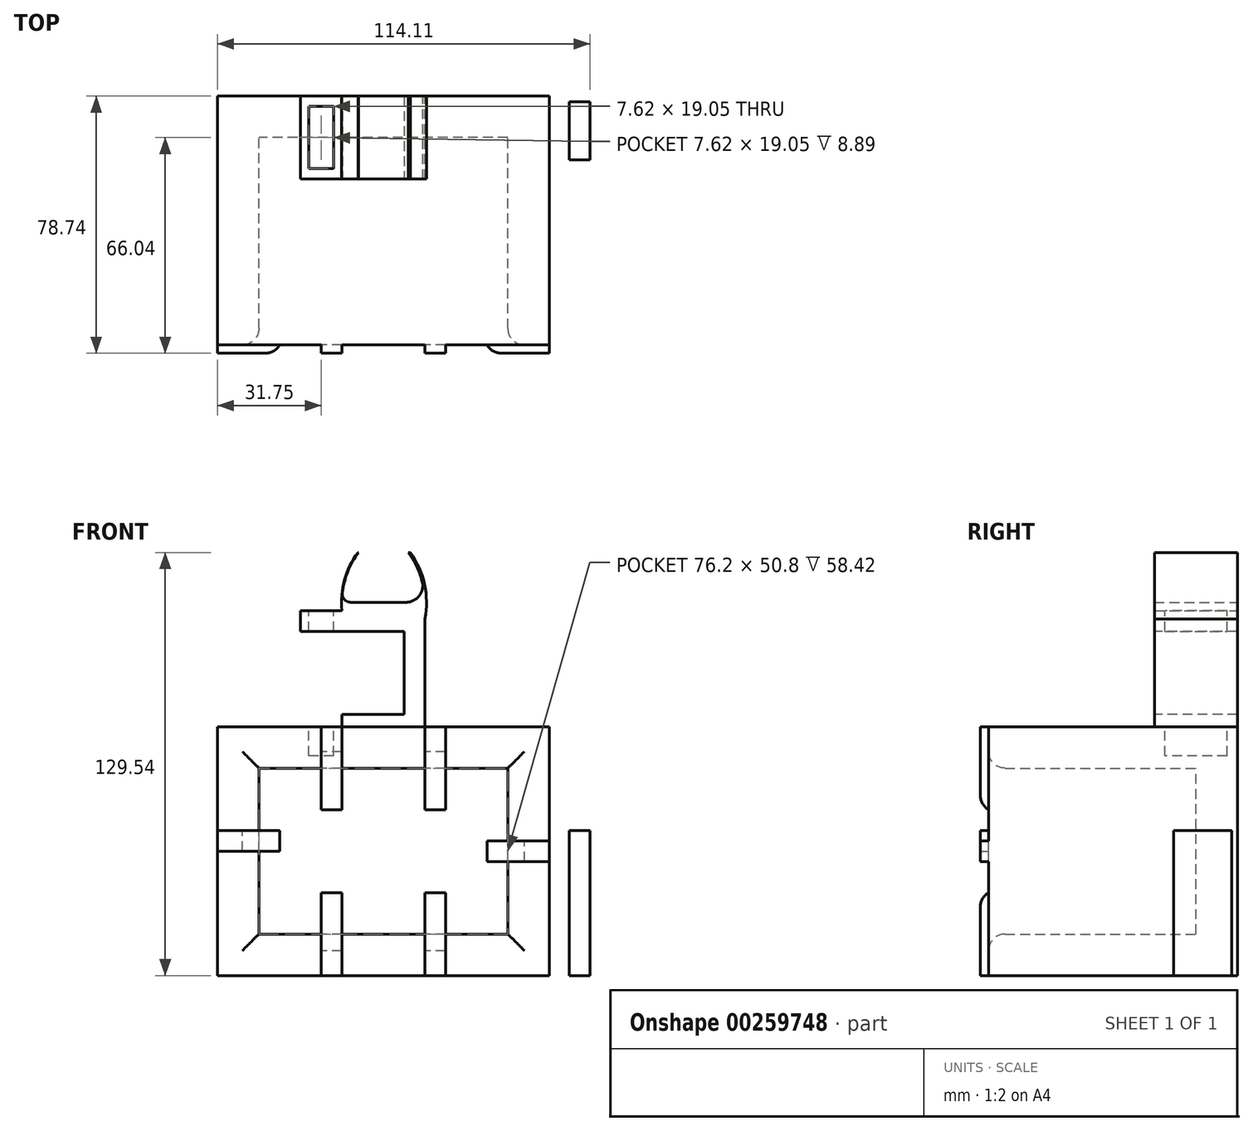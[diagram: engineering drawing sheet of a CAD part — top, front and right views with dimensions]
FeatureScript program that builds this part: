
annotation { "Feature Type Name" : "Feature", "Feature Type Description" : "" }
export const myFeature = defineFeature(function(context is Context, id is Id, definition is map)
    precondition{}
    {
        {
            var Q0;
            Q0=qCreatedBy(makeId("Front.planeOp"),FACE);
            var sketch = newSketch(context, id + "F0", { "sketchPlane" : qUnion([Q0])});
            skLineSegment(sketch, "E0.bottom", {"start": v(0, 0) * mm, "end": v(-101.6, 0) * mm});
            skLineSegment(sketch, "E0.top", {"start": v(0, 76.2) * mm, "end": v(-101.6, 76.2) * mm});
            skLineSegment(sketch, "E0.left", {"start": v(0, 0) * mm, "end": v(0, 76.2) * mm});
            skLineSegment(sketch, "E0.right", {"start": v(-101.6, 0) * mm, "end": v(-101.6, 76.2) * mm});
            skSolve(sketch);
        }
        {
            var Q0;
            Q0=makeQuery(id+"F0.imprint","IMPRINT",FACE,{"disambiguationData":[TD([[makeQuery(id+"F0.imprint","IMPRINT",EDGE,{"derivedFrom":sQuery(id+"F0.wireOp",EDGE,"E0.bottom")}),-1.0]])]});
            extrude(context, id + "F1", {"entities" : qUnion([Q0]), "depth" : 76.2 * mm});
        }
        {
            var Q0;
            Q0=makeQuery(id+"F1.opExtrude","CAP_FACE",FACE,{"disambiguationData":[OSD([sQuery(id+"F0.wireOp",EDGE,"E0.bottom"),sQuery(id+"F0.wireOp",EDGE,"E0.top"),sQuery(id+"F0.wireOp",EDGE,"E0.left"),sQuery(id+"F0.wireOp",EDGE,"E0.right")])],"isStart":false});
            shell(context, id + "F2", {"entities" : qUnion([Q0]), "thickness" : 12.7 * mm});
        }
        {
            var Q0;
            {var subQ0=sQuery(id+"F0.wireOp",EDGE,"E0.right");Q0=makeQuery(id+"F2.opShell","OFFSET_EDGE",EDGE,{"disambiguationData":[OSD([subQ0]),TDD([makeQuery(id+"F1.opExtrude","CAP_EDGE",EDGE,{"disambiguationData":[OSD([subQ0])],"isStart":false})])]});}
            var Q1;
            {var subQ0=sQuery(id+"F0.wireOp",EDGE,"E0.top");Q1=makeQuery(id+"F2.opShell","OFFSET_EDGE",EDGE,{"disambiguationData":[OSD([subQ0]),TDD([makeQuery(id+"F1.opExtrude","CAP_EDGE",EDGE,{"disambiguationData":[OSD([subQ0])],"isStart":false})])]});}
            var Q2;
            {var subQ0=sQuery(id+"F0.wireOp",EDGE,"E0.left");Q2=makeQuery(id+"F2.opShell","OFFSET_EDGE",EDGE,{"disambiguationData":[OSD([subQ0]),TDD([makeQuery(id+"F1.opExtrude","CAP_EDGE",EDGE,{"disambiguationData":[OSD([subQ0])],"isStart":false})])]});}
            var Q3;
            {var subQ0=sQuery(id+"F0.wireOp",EDGE,"E0.bottom");Q3=makeQuery(id+"F2.opShell","OFFSET_EDGE",EDGE,{"disambiguationData":[OSD([subQ0]),TDD([makeQuery(id+"F1.opExtrude","CAP_EDGE",EDGE,{"disambiguationData":[OSD([subQ0])],"isStart":false})])]});}
            fillet(context, id + "F3", {"entities" : qUnion([Q0, Q1, Q2, Q3]), "radius" : 5.08 * mm, "tangentPropagation" : true, "allowEdgeOverflow" : false});
        }
        {
            var Q0;
            Q0=makeQuery(id+"F1.opExtrude","CAP_FACE",FACE,{"disambiguationData":[OSD([sQuery(id+"F0.wireOp",EDGE,"E0.bottom"),sQuery(id+"F0.wireOp",EDGE,"E0.top"),sQuery(id+"F0.wireOp",EDGE,"E0.left"),sQuery(id+"F0.wireOp",EDGE,"E0.right")])],"isStart":false});
            var sketch = newSketch(context, id + "F4", { "sketchPlane" : qUnion([Q0])});
            skLineSegment(sketch, "E1.bottom", {"start": v(-69.85, 76.2) * mm, "end": v(-63.5, 76.2) * mm});
            skLineSegment(sketch, "E1.top", {"start": v(-69.85, 50.8) * mm, "end": v(-63.5, 50.8) * mm});
            skLineSegment(sketch, "E1.left", {"start": v(-69.85, 76.2) * mm, "end": v(-69.85, 50.8) * mm});
            skLineSegment(sketch, "E1.right", {"start": v(-63.5, 76.2) * mm, "end": v(-63.5, 50.8) * mm});
            skLineSegment(sketch, "E2.bottom", {"start": v(-38.1, 76.2) * mm, "end": v(-31.75, 76.2) * mm});
            skLineSegment(sketch, "E2.top", {"start": v(-38.1, 50.8) * mm, "end": v(-31.75, 50.8) * mm});
            skLineSegment(sketch, "E2.left", {"start": v(-38.1, 76.2) * mm, "end": v(-38.1, 50.8) * mm});
            skLineSegment(sketch, "E2.right", {"start": v(-31.75, 76.2) * mm, "end": v(-31.75, 50.8) * mm});
            skLineSegment(sketch, "E3.bottom", {"start": v(-101.6, 38.1) * mm, "end": v(-82.55, 38.1) * mm});
            skLineSegment(sketch, "E3.top", {"start": v(-101.6, 44.45) * mm, "end": v(-82.55, 44.45) * mm});
            skLineSegment(sketch, "E3.left", {"start": v(-101.6, 38.1) * mm, "end": v(-101.6, 44.45) * mm});
            skLineSegment(sketch, "E3.right", {"start": v(-82.55, 38.1) * mm, "end": v(-82.55, 44.45) * mm});
            skLineSegment(sketch, "E4.bottom", {"start": v(-12.7, 41.27) * mm, "end": v(0, 41.27) * mm});
            skLineSegment(sketch, "E4.top", {"start": v(-19.05, 34.92) * mm, "end": v(0, 34.92) * mm});
            skLineSegment(sketch, "E4.right", {"start": v(0, 41.27) * mm, "end": v(0, 34.92) * mm});
            skLineSegment(sketch, "E5.bottom", {"start": v(-69.85, 0) * mm, "end": v(-63.5, 0) * mm});
            skLineSegment(sketch, "E5.top", {"start": v(-69.85, 25.4) * mm, "end": v(-63.5, 25.4) * mm});
            skLineSegment(sketch, "E5.left", {"start": v(-69.85, 0) * mm, "end": v(-69.85, 25.4) * mm});
            skLineSegment(sketch, "E5.right", {"start": v(-63.5, 0) * mm, "end": v(-63.5, 25.4) * mm});
            skLineSegment(sketch, "E6.bottom", {"start": v(-38.1, 25.4) * mm, "end": v(-31.75, 25.4) * mm});
            skLineSegment(sketch, "E6.top", {"start": v(-38.1, 0) * mm, "end": v(-31.75, 0) * mm});
            skLineSegment(sketch, "E6.left", {"start": v(-38.1, 25.4) * mm, "end": v(-38.1, 0) * mm});
            skLineSegment(sketch, "E6.right", {"start": v(-31.75, 25.4) * mm, "end": v(-31.75, 0) * mm});
            skLineSegment(sketch, "E7", {"start": v(-12.7, 41.27) * mm, "end": v(-19.05, 41.27) * mm});
            skLineSegment(sketch, "E8", {"start": v(-19.05, 41.27) * mm, "end": v(-19.05, 34.92) * mm});
            skSolve(sketch);
        }
        {
            var Q0;
            Q0 = qSketchRegion(id + "F4", true);
            extrude(context, id + "F5", {"entities" : qUnion([Q0]), "operationType" : NewBodyOperationType.ADD, "depth" : 2.54 * mm});
        }
        {
            var Q0;
            Q0=makeQuery(id+"F5.opExtrude","CAP_EDGE",EDGE,{"disambiguationData":[OSD([sQuery(id+"F4.wireOp",EDGE,"E3.right")])],"isStart":false});
            var Q1;
            Q1=makeQuery(id+"F5.opExtrude","CAP_EDGE",EDGE,{"disambiguationData":[OSD([sQuery(id+"F4.wireOp",EDGE,"E1.top")])],"isStart":false});
            var Q2;
            Q2=makeQuery(id+"F5.opExtrude","CAP_EDGE",EDGE,{"disambiguationData":[OSD([sQuery(id+"F4.wireOp",EDGE,"E2.top")])],"isStart":false});
            var Q3;
            Q3=makeQuery(id+"F5.opExtrude","CAP_EDGE",EDGE,{"disambiguationData":[OSD([sQuery(id+"F4.wireOp",EDGE,"E8")])],"isStart":false});
            var Q4;
            Q4=makeQuery(id+"F5.opExtrude","CAP_EDGE",EDGE,{"disambiguationData":[OSD([sQuery(id+"F4.wireOp",EDGE,"E6.bottom")])],"isStart":false});
            var Q5;
            Q5=makeQuery(id+"F5.opExtrude","CAP_EDGE",EDGE,{"disambiguationData":[OSD([sQuery(id+"F4.wireOp",EDGE,"E5.top")])],"isStart":false});
            fillet(context, id + "F6", {"entities" : qUnion([Q0, Q1, Q2, Q3, Q4, Q5]), "radius" : 5.08 * mm, "tangentPropagation" : true, "allowEdgeOverflow" : false});
        }
        {
            var Q0;
            Q0=makeQuery(id+"F1.opExtrude","CAP_FACE",FACE,{"disambiguationData":[OSD([sQuery(id+"F0.wireOp",EDGE,"E0.bottom"),sQuery(id+"F0.wireOp",EDGE,"E0.top"),sQuery(id+"F0.wireOp",EDGE,"E0.left"),sQuery(id+"F0.wireOp",EDGE,"E0.right")])],"isStart":true});
            var sketch = newSketch(context, id + "F7", { "sketchPlane" : qUnion([Q0])});
            skLineSegment(sketch, "E9.bottom", {"start": v(38.1, 76.2) * mm, "end": v(63.5, 76.2) * mm});
            skLineSegment(sketch, "E9.top", {"start": v(38.1, 114.3) * mm, "end": v(63.5, 114.3) * mm});
            skLineSegment(sketch, "E9.left", {"start": v(38.1, 76.2) * mm, "end": v(38.1, 114.3) * mm});
            skLineSegment(sketch, "E9.right", {"start": v(63.5, 76.2) * mm, "end": v(63.5, 114.3) * mm});
            skSolve(sketch);
        }
        {
            var Q0;
            Q0 = qSketchRegion(id + "F7", true);
            extrude(context, id + "F8", {"entities" : qUnion([Q0]), "operationType" : NewBodyOperationType.ADD, "oppositeDirection" : true, "depth" : 25.4 * mm});
        }
        {
            var Q0;
            Q0=makeQuery(id+"F8.opExtrude","SWEPT_FACE",FACE,{"disambiguationData":[OSD([sQuery(id+"F7.wireOp",EDGE,"E9.right")])]});
            var sketch = newSketch(context, id + "F9", { "sketchPlane" : qUnion([Q0])});
            skLineSegment(sketch, "E10.bottom", {"start": v(25.4, 114.3) * mm, "end": v(0, 114.3) * mm});
            skLineSegment(sketch, "E10.top", {"start": v(25.4, 111.76) * mm, "end": v(0, 111.76) * mm});
            skLineSegment(sketch, "E10.left", {"start": v(25.4, 114.3) * mm, "end": v(25.4, 111.76) * mm});
            skLineSegment(sketch, "E10.right", {"start": v(0, 114.3) * mm, "end": v(0, 111.76) * mm});
            skSolve(sketch);
        }
        {
            var Q0;
            Q0 = qSketchRegion(id + "F9", true);
            var Q1;
            Q1=makeQuery(id+"F8.opExtrude","SWEPT_EDGE",EDGE,{"disambiguationData":[OSD([sQuery(id+"F7.wireOp",EDGE,"E9.top"),sQuery(id+"F7.wireOp",EDGE,"E9.left")])]});
            revolve(context, id + "F10", {"operationType" : NewBodyOperationType.ADD, "entities" : qUnion([Q0]), "axis" : qUnion([Q1]), "revolveType" : RevolveType.ONE_DIRECTION, "angle" : 45 * degree});
        }
        {
            var Q0;
            Q0=makeQuery(id+"F8.opExtrude","SWEPT_FACE",FACE,{"disambiguationData":[OSD([sQuery(id+"F7.wireOp",EDGE,"E9.left")])]});
            var sketch = newSketch(context, id + "F11", { "sketchPlane" : qUnion([Q0])});
            skLineSegment(sketch, "E11.bottom", {"start": v(-25.4, 114.3) * mm, "end": v(0, 114.3) * mm});
            skLineSegment(sketch, "E11.top", {"start": v(-25.4, 109.22) * mm, "end": v(0, 109.22) * mm});
            skLineSegment(sketch, "E11.left", {"start": v(-25.4, 114.3) * mm, "end": v(-25.4, 109.22) * mm});
            skLineSegment(sketch, "E11.right", {"start": v(0, 114.3) * mm, "end": v(0, 109.22) * mm});
            skSolve(sketch);
        }
        {
            var Q0;
            Q0 = qSketchRegion(id + "F11", true);
            var Q1;
            Q1=makeQuery(id+"F8.opExtrude","SWEPT_EDGE",EDGE,{"disambiguationData":[OSD([sQuery(id+"F7.wireOp",EDGE,"E9.top"),sQuery(id+"F7.wireOp",EDGE,"E9.right")])]});
            revolve(context, id + "F12", {"operationType" : NewBodyOperationType.ADD, "entities" : qUnion([Q0]), "axis" : qUnion([Q1]), "revolveType" : RevolveType.ONE_DIRECTION, "oppositeDirection" : true, "angle" : 60 * degree});
        }
        {
            var Q0;
            Q0=makeQuery(id+"F8.opExtrude","SWEPT_FACE",FACE,{"disambiguationData":[OSD([sQuery(id+"F7.wireOp",EDGE,"E9.top")])]});
            extrude(context, id + "F13", {"entities" : qUnion([Q0]), "operationType" : NewBodyOperationType.REMOVE, "depth" : 25.4 * mm, "hasSecondDirection" : true, "secondDirectionOppositeDirection" : false, "secondDirectionDepth" : 15.24 * mm});
        }
        {
            var Q0;
            Q0=makeQuery(id+"F10.boolean.opBoolean","MERGE",EDGE,{"derivedFrom":[makeQuery(id+"F8.opExtrude","SWEPT_EDGE",EDGE,{"disambiguationData":[OSD([sQuery(id+"F7.wireOp",EDGE,"E9.top"),sQuery(id+"F7.wireOp",EDGE,"E9.right")])]}),makeQuery(id+"F10.opRevolve","CAP_EDGE",EDGE,{"disambiguationData":[OSD([sQuery(id+"F9.wireOp",EDGE,"E10.bottom")]),OD(0.0)],"isStart":false})]});
            fillet(context, id + "F14", {"entities" : qUnion([Q0]), "radius" : 2.54 * mm, "tangentPropagation" : true, "allowEdgeOverflow" : false});
        }
        {
            var Q0;
            Q0=makeQuery(id+"F12.boolean.opBoolean","MERGE",EDGE,{"derivedFrom":[makeQuery(id+"F8.opExtrude","SWEPT_EDGE",EDGE,{"disambiguationData":[OSD([sQuery(id+"F7.wireOp",EDGE,"E9.top"),sQuery(id+"F7.wireOp",EDGE,"E9.left")])]}),makeQuery(id+"F12.opRevolve","CAP_EDGE",EDGE,{"disambiguationData":[OSD([sQuery(id+"F11.wireOp",EDGE,"E11.bottom")]),OD(0.0)],"isStart":false})]});
            fillet(context, id + "F15", {"entities" : qUnion([Q0]), "radius" : 5.08 * mm, "tangentPropagation" : true, "allowEdgeOverflow" : false});
        }
        {
            var Q0;
            Q0=makeQuery(id+"F8.opExtrude","SWEPT_FACE",FACE,{"disambiguationData":[OSD([sQuery(id+"F7.wireOp",EDGE,"E9.right")])]});
            var sketch = newSketch(context, id + "F16", { "sketchPlane" : qUnion([Q0])});
            skLineSegment(sketch, "E12.bottom", {"start": v(0, 80) * mm, "end": v(25.4, 80) * mm});
            skLineSegment(sketch, "E12.top", {"start": v(0, 105.4) * mm, "end": v(25.4, 105.4) * mm});
            skLineSegment(sketch, "E12.left", {"start": v(0, 80) * mm, "end": v(0, 105.4) * mm});
            skLineSegment(sketch, "E12.right", {"start": v(25.4, 80) * mm, "end": v(25.4, 105.4) * mm});
            skSolve(sketch);
        }
        {
            var Q0;
            Q0 = qSketchRegion(id + "F16", true);
            extrude(context, id + "F17", {"entities" : qUnion([Q0]), "operationType" : NewBodyOperationType.REMOVE, "oppositeDirection" : true, "depth" : 19.05 * mm});
        }
        {
            var Q0;
            {var subQ0=sQuery(id+"F7.wireOp",EDGE,"E9.right");Q0=makeQuery(id+"F17.boolean.opBoolean","SPLIT",FACE,{"disambiguationData":[TD([makeQuery(id+"F10.opRevolve","SWEPT_FACE",FACE,{"disambiguationData":[OSD([sQuery(id+"F9.wireOp",EDGE,"E10.top")])]})])],"derivedFrom":makeQuery(id+"F8.opExtrude","SWEPT_FACE",FACE,{"disambiguationData":[OSD([subQ0])]})});}
            extrude(context, id + "F18", {"entities" : qUnion([Q0]), "operationType" : NewBodyOperationType.ADD, "depth" : 12.7 * mm});
        }
        {
            var Q0;
            Q0=makeQuery(id+"F18.opExtrude","SWEPT_FACE",FACE,{"disambiguationData":[OSD([sQuery(id+"F9.wireOp",EDGE,"E10.top")])]});
            var sketch = newSketch(context, id + "F19", { "sketchPlane" : qUnion([Q0])});
            skCircle(sketch, "E13", {"center": v(-69.85, -12.7) * mm, "radius": 3.81 * mm});
            skLineSegment(sketch, "E14.bottom", {"start": v(-66.04, -3.18) * mm, "end": v(-73.66, -3.18) * mm});
            skLineSegment(sketch, "E14.top", {"start": v(-66.04, -22.23) * mm, "end": v(-73.66, -22.23) * mm});
            skLineSegment(sketch, "E14.left", {"start": v(-66.04, -3.18) * mm, "end": v(-66.04, -22.23) * mm});
            skLineSegment(sketch, "E14.right", {"start": v(-73.66, -3.18) * mm, "end": v(-73.66, -22.23) * mm});
            skSolve(sketch);
        }
        {
            var Q0;
            Q0 = qSketchRegion(id + "F19", true);
            extrude(context, id + "F20", {"entities" : qUnion([Q0]), "operationType" : NewBodyOperationType.REMOVE, "oppositeDirection" : true, "depth" : 44.45 * mm});
        }
        {
            var Q0;
            Q0=qCreatedBy(makeId("Top.planeOp"),FACE);
            var sketch = newSketch(context, id + "F21", { "sketchPlane" : qUnion([Q0])});
            skLineSegment(sketch, "E15.bottom", {"start": v(12.5, -19.56) * mm, "end": v(6.16, -19.56) * mm});
            skLineSegment(sketch, "E15.top", {"start": v(12.5, -1.78) * mm, "end": v(6.16, -1.78) * mm});
            skLineSegment(sketch, "E15.left", {"start": v(12.5, -19.56) * mm, "end": v(12.5, -1.78) * mm});
            skLineSegment(sketch, "E15.right", {"start": v(6.16, -19.56) * mm, "end": v(6.16, -1.78) * mm});
            skPoint(sketch, "E15.middle", {"position": v(9.33, -10.67) * mm});
            skSolve(sketch);
        }
        {
            var Q0;
            Q0 = qSketchRegion(id + "F21", true);
            extrude(context, id + "F22", {"entities" : qUnion([Q0]), "depth" : 44.45 * mm});
        }
    });
